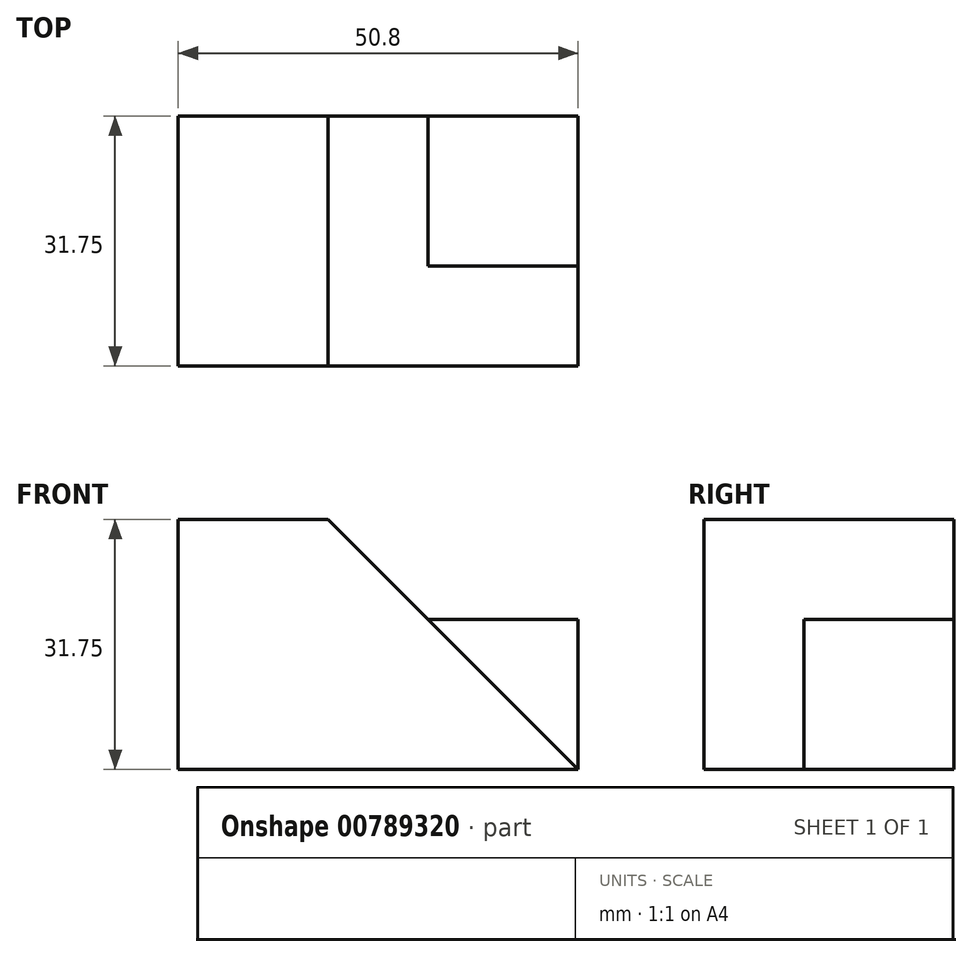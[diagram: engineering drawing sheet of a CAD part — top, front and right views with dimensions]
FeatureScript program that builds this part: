
annotation { "Feature Type Name" : "Feature", "Feature Type Description" : "" }
export const myFeature = defineFeature(function(context is Context, id is Id, definition is map)
    precondition{}
    {
        {
            var Q0;
            Q0=qCreatedBy(makeId("Front.planeOp"),FACE);
            var sketch = newSketch(context, id + "F0", { "sketchPlane" : qUnion([Q0])});
            skLineSegment(sketch, "E0", {"start": v(0, 0) * mm, "end": v(50.8, 0) * mm});
            skLineSegment(sketch, "E1", {"start": v(50.8, 0) * mm, "end": v(50.8, 31.75) * mm});
            skLineSegment(sketch, "E2", {"start": v(50.8, 31.75) * mm, "end": v(0, 31.75) * mm});
            skLineSegment(sketch, "E3", {"start": v(0, 31.75) * mm, "end": v(0, 0) * mm});
            skSolve(sketch);
        }
        {
            var Q0;
            Q0=makeQuery(id+"F0.imprint","IMPRINT",FACE,{"disambiguationData":[TD([[makeQuery(id+"F0.imprint","IMPRINT",EDGE,{"derivedFrom":sQuery(id+"F0.wireOp",EDGE,"E0")}),1.0]])]});
            extrude(context, id + "F1", {"entities" : qUnion([Q0]), "depth" : 31.75 * mm, "offsetDistance" : 25.4 * mm});
        }
        {
            var Q0;
            Q0=makeQuery(id+"F1.opExtrude","CAP_FACE",FACE,{"disambiguationData":[OSD([sQuery(id+"F0.wireOp",EDGE,"E0"),sQuery(id+"F0.wireOp",EDGE,"E1"),sQuery(id+"F0.wireOp",EDGE,"E2"),sQuery(id+"F0.wireOp",EDGE,"E3")])],"isStart":false});
            var sketch = newSketch(context, id + "F2", { "sketchPlane" : qUnion([Q0])});
            skLineSegment(sketch, "E4", {"start": v(50.8, 0) * mm, "end": v(50.8, 19.05) * mm});
            skLineSegment(sketch, "E5", {"start": v(50.8, 19.05) * mm, "end": v(31.75, 19.05) * mm});
            skLineSegment(sketch, "E6", {"start": v(31.75, 19.05) * mm, "end": v(50.8, 0) * mm});
            skLineSegment(sketch, "E7", {"start": v(31.75, 19.05) * mm, "end": v(19.05, 31.75) * mm});
            skSolve(sketch);
        }
        {
            var Q0;
            {var subQ0=sQuery(id+"F2.wireOp",EDGE,"E5");Q0=makeQuery(id+"F2.imprint","IMPRINT",FACE,{"disambiguationData":[TD([[makeQuery(id+"F2.imprint","IMPRINT",EDGE,{"derivedFrom":subQ0}),-1.0]])]});}
            extrude(context, id + "F3", {"entities" : qUnion([Q0]), "operationType" : NewBodyOperationType.REMOVE, "endBound" : BoundingType.UP_TO_NEXT, "oppositeDirection" : true, "depth" : 25.4 * mm, "offsetDistance" : 25.4 * mm});
        }
        {
            var Q0;
            Q0=makeQuery(id+"F1.opExtrude","CAP_FACE",FACE,{"disambiguationData":[OSD([sQuery(id+"F0.wireOp",EDGE,"E0"),sQuery(id+"F0.wireOp",EDGE,"E1"),sQuery(id+"F0.wireOp",EDGE,"E2"),sQuery(id+"F0.wireOp",EDGE,"E3")])],"isStart":false});
            var sketch = newSketch(context, id + "F4", { "sketchPlane" : qUnion([Q0])});
            skLineSegment(sketch, "E8", {"start": v(31.75, 19.05) * mm, "end": v(50.8, 0) * mm});
            skSolve(sketch);
        }
        {
            var Q0;
            Q0=makeQuery(id+"F4.imprint","IMPRINT",FACE,{"disambiguationData":[TD([[makeQuery(id+"F4.imprint","IMPRINT",EDGE,{"derivedFrom":sQuery(id+"F4.wireOp",EDGE,"E8")}),1.0]])]});
            extrude(context, id + "F5", {"entities" : qUnion([Q0]), "operationType" : NewBodyOperationType.REMOVE, "oppositeDirection" : true, "depth" : 12.7 * mm, "offsetDistance" : 25.4 * mm});
        }
    });
